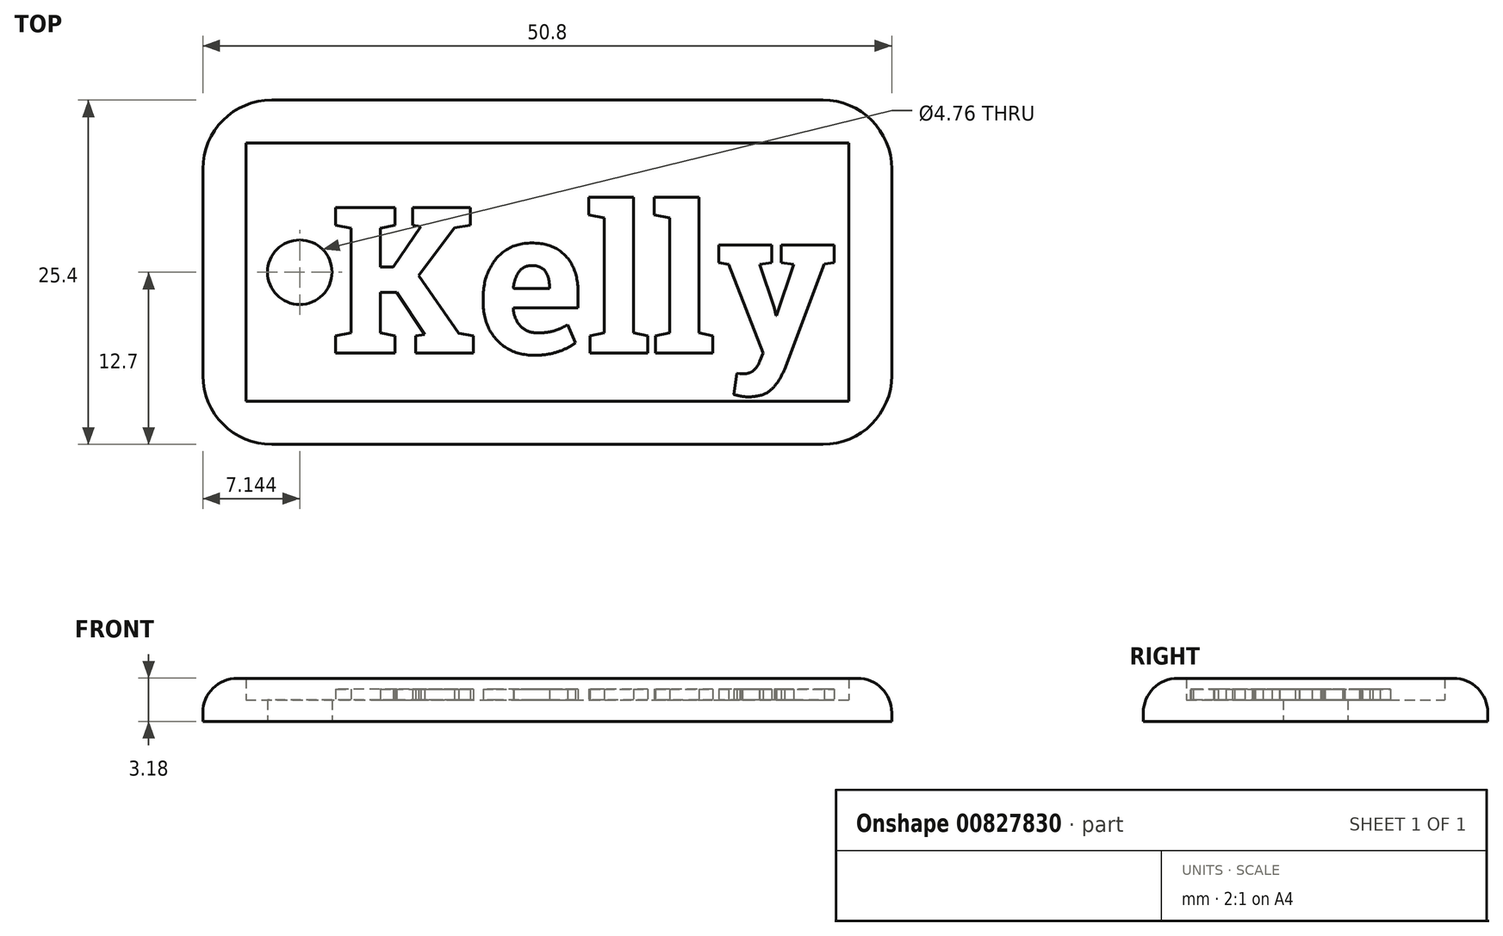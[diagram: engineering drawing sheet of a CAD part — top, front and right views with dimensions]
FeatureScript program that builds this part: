
annotation { "Feature Type Name" : "Feature", "Feature Type Description" : "" }
export const myFeature = defineFeature(function(context is Context, id is Id, definition is map)
    precondition{}
    {
        {
            var Q0;
            Q0=qCreatedBy(makeId("Top.planeOp"),FACE);
            var sketch = newSketch(context, id + "F0", { "sketchPlane" : qUnion([Q0])});
            skLineSegment(sketch, "E0.bottom", {"start": v(0, 0) * mm, "end": v(50.8, 0) * mm});
            skLineSegment(sketch, "E0.top", {"start": v(0, 25.4) * mm, "end": v(50.8, 25.4) * mm});
            skLineSegment(sketch, "E0.left", {"start": v(0, 0) * mm, "end": v(0, 25.4) * mm});
            skLineSegment(sketch, "E0.right", {"start": v(50.8, 0) * mm, "end": v(50.8, 25.4) * mm});
            skCircle(sketch, "E1", {"center": v(7.14, 12.7) * mm, "radius": 2.38 * mm});
            skPoint(sketch, "E1.centerSnap0", {"position": v(0, 12.7) * mm});
            skLineSegment(sketch, "E2.0", {"start": v(3.18, 22.23) * mm, "end": v(47.62, 22.23) * mm});
            skLineSegment(sketch, "E2.1", {"start": v(3.18, 3.18) * mm, "end": v(3.17, 22.22) * mm});
            skLineSegment(sketch, "E2.2", {"start": v(3.18, 3.18) * mm, "end": v(47.62, 3.18) * mm});
            skLineSegment(sketch, "E2.3", {"start": v(47.62, 3.18) * mm, "end": v(47.62, 22.23) * mm});
            skSolve(sketch);
        }
        {
            var Q0;
            Q0=makeQuery(id+"F0.imprint","IMPRINT",FACE,{"disambiguationData":[TD([[makeQuery(id+"F0.imprint","IMPRINT",EDGE,{"derivedFrom":sQuery(id+"F0.wireOp",EDGE,"E1")}),-1.0]])]});
            extrude(context, id + "F1", {"entities" : qUnion([Q0]), "depth" : 1.59 * mm, "offsetDistance" : 25.4 * mm});
        }
        {
            var Q0;
            Q0 = qSketchRegion(id + "F0", true);
            extrude(context, id + "F2", {"entities" : qUnion([Q0]), "operationType" : NewBodyOperationType.ADD, "depth" : 3.17 * mm, "offsetDistance" : 25.4 * mm});
        }
        {
            var Q0;
            Q0=makeQuery(id+"F2.opExtrude","SWEPT_EDGE",EDGE,{"disambiguationData":[OSD([sQuery(id+"F0.wireOp",EDGE,"E0.bottom"),sQuery(id+"F0.wireOp",EDGE,"E0.right")])]});
            var Q1;
            Q1=makeQuery(id+"F2.opExtrude","SWEPT_EDGE",EDGE,{"disambiguationData":[OSD([sQuery(id+"F0.wireOp",EDGE,"E0.bottom"),sQuery(id+"F0.wireOp",EDGE,"E0.left")])]});
            var Q2;
            Q2=makeQuery(id+"F2.opExtrude","SWEPT_EDGE",EDGE,{"disambiguationData":[OSD([sQuery(id+"F0.wireOp",EDGE,"E0.top"),sQuery(id+"F0.wireOp",EDGE,"E0.right")])]});
            var Q3;
            Q3=makeQuery(id+"F2.opExtrude","SWEPT_EDGE",EDGE,{"disambiguationData":[OSD([sQuery(id+"F0.wireOp",EDGE,"E0.top"),sQuery(id+"F0.wireOp",EDGE,"E0.left")])]});
            fillet(context, id + "F3", {"entities" : qUnion([Q0, Q1, Q2, Q3]), "radius" : 5.08 * mm, "tangentPropagation" : true, "allowEdgeOverflow" : false});
        }
        {
            var Q0;
            Q0=makeQuery(id+"F2.opExtrude","CAP_EDGE",EDGE,{"disambiguationData":[OSD([sQuery(id+"F0.wireOp",EDGE,"E0.bottom")])],"isStart":false});
            fillet(context, id + "F4", {"entities" : qUnion([Q0]), "radius" : 2.54 * mm, "tangentPropagation" : true, "allowEdgeOverflow" : false});
        }
        {
            var Q0;
            Q0=qCreatedBy(makeId("Top.planeOp"),FACE);
            var sketch = newSketch(context, id + "F5", { "sketchPlane" : qUnion([Q0])});
            skText(sketch, "E3", { "text": "Kelly", "fontName": "RobotoSlab-Bold.ttf"});
            const initialGuessF5  = {"E3": [0.00938, 0.00673, 1, 0, 0.01087]};
            skSetInitialGuess(sketch, initialGuessF5);
            skSolve(sketch);
        }
        {
            var Q0;
            Q0 = qSketchRegion(id + "F5", true);
            extrude(context, id + "F6", {"entities" : qUnion([Q0]), "operationType" : NewBodyOperationType.ADD, "depth" : 2.38 * mm, "offsetDistance" : 25.4 * mm});
        }
    });
